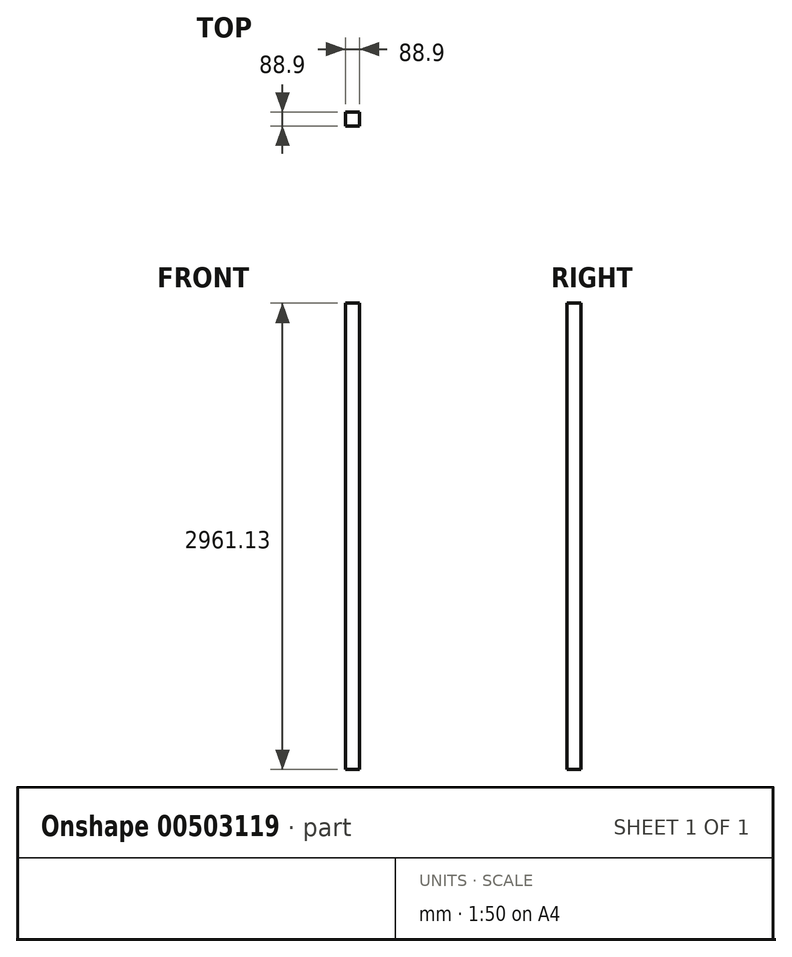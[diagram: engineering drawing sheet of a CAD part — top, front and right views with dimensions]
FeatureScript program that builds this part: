
annotation { "Feature Type Name" : "Feature", "Feature Type Description" : "" }
export const myFeature = defineFeature(function(context is Context, id is Id, definition is map)
    precondition{}
    {
        {
            var Q0;
            Q0=qCreatedBy(makeId("Top.planeOp"),FACE);
            var sketch = newSketch(context, id + "F0", { "sketchPlane" : qUnion([Q0])});
            skLineSegment(sketch, "E0.bottom", {"start": v(0, 0) * mm, "end": v(88.9, 0) * mm});
            skLineSegment(sketch, "E0.top", {"start": v(0, 88.9) * mm, "end": v(88.9, 88.9) * mm});
            skLineSegment(sketch, "E0.left", {"start": v(0, 0) * mm, "end": v(0, 88.9) * mm});
            skLineSegment(sketch, "E0.right", {"start": v(88.9, 0) * mm, "end": v(88.9, 88.9) * mm});
            skSolve(sketch);
        }
        {
            var Q0;
            Q0 = qSketchRegion(id + "F0", true);
            extrude(context, id + "F1", {"entities" : qUnion([Q0]), "depth" : 2961.13 * mm});
        }
    });
